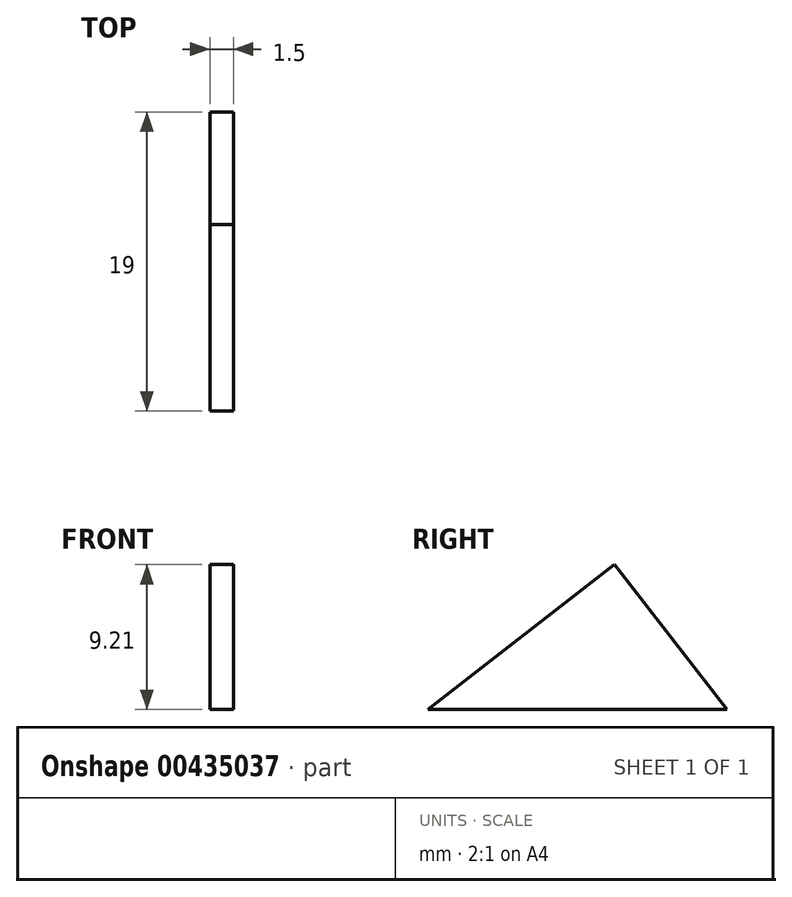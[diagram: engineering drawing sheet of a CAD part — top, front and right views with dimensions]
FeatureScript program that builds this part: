
annotation { "Feature Type Name" : "Feature", "Feature Type Description" : "" }
export const myFeature = defineFeature(function(context is Context, id is Id, definition is map)
    precondition{}
    {
        {
            var Q0;
            Q0=qCreatedBy(makeId("Right.planeOp"),FACE);
            var sketch = newSketch(context, id + "F0", { "sketchPlane" : qUnion([Q0])});
            skLineSegment(sketch, "E0", {"start": v(0, 0) * mm, "end": v(11.84, 9.2) * mm});
            skLineSegment(sketch, "E1", {"start": v(11.84, 9.2) * mm, "end": v(19, 0) * mm});
            skLineSegment(sketch, "E2", {"start": v(19, 0) * mm, "end": v(0, 0) * mm});
            skSolve(sketch);
        }
        {
            var Q0;
            Q0 = qSketchRegion(id + "F0", true);
            extrude(context, id + "F1", {"entities" : qUnion([Q0]), "depth" : 1.5 * mm});
        }
    });
